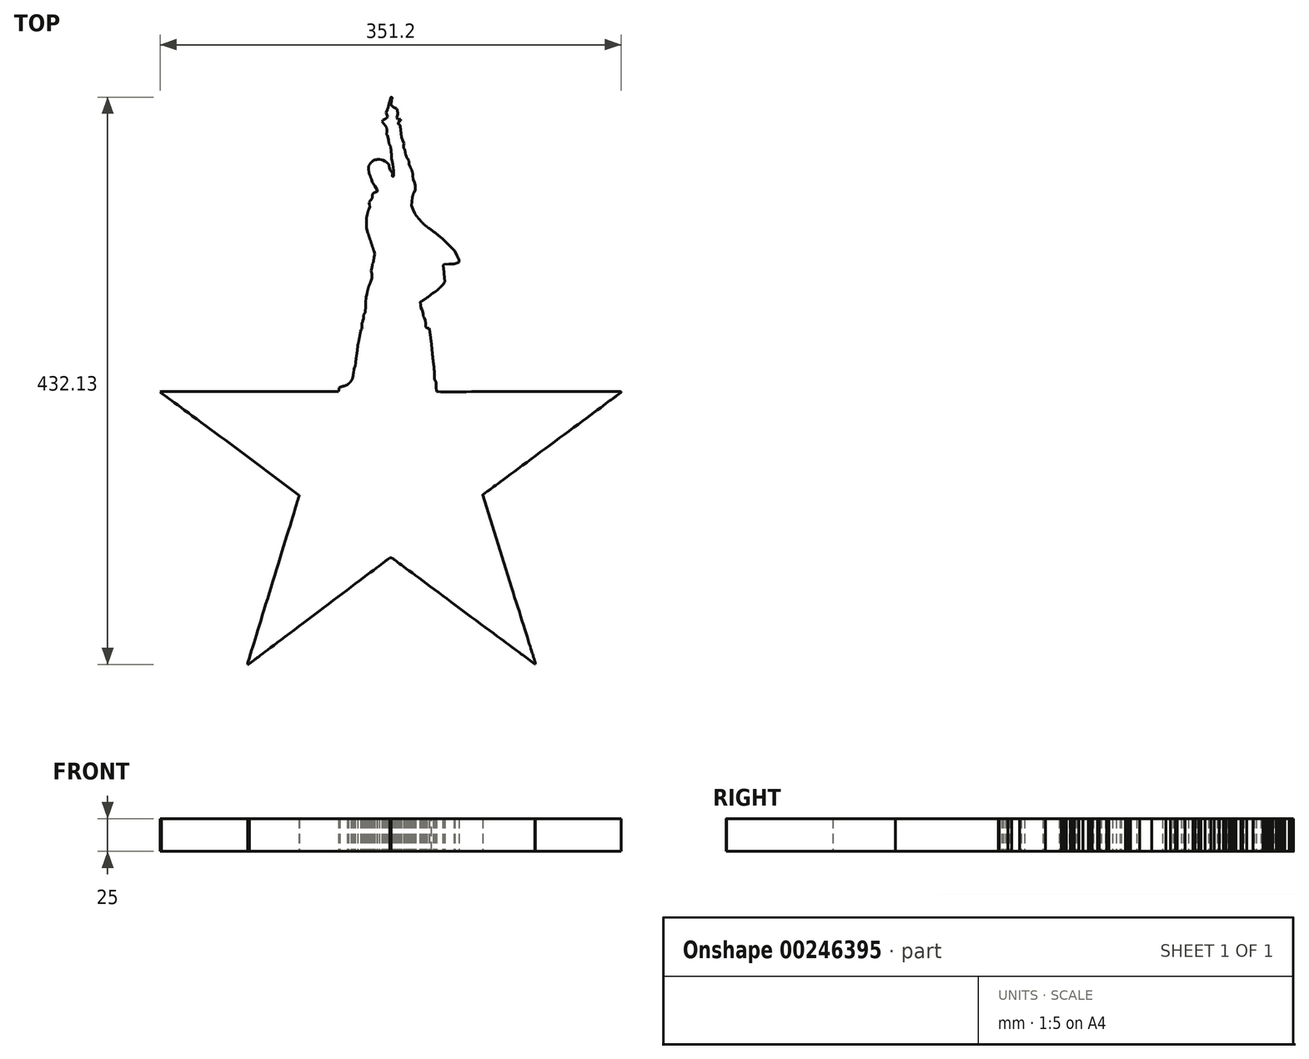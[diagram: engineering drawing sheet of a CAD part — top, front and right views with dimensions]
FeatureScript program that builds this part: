
annotation { "Feature Type Name" : "Feature", "Feature Type Description" : "" }
export const myFeature = defineFeature(function(context is Context, id is Id, definition is map)
    precondition{}
    {
        {
            var Q0;
            Q0=qCreatedBy(makeId("Top.planeOp"),FACE);
            var sketch = newSketch(context, id + "F0", { "sketchPlane" : qUnion([Q0])});
            skFitSpline(sketch, "E0", {"points": [v(0.01, 215.25) * mm, v(-0.13, 214.87) * mm, v(-0.43, 213.8) * mm, v(-0.75, 212.7) * mm]});
            skFitSpline(sketch, "E1", {"points": [v(-0.75, 212.7) * mm, v(-1.07, 211.6) * mm, v(-1.41, 210.33) * mm, v(-1.5, 209.87) * mm]});
            skFitSpline(sketch, "E2", {"points": [v(-1.5, 209.87) * mm, v(-1.6, 209.4) * mm, v(-2.07, 207.96) * mm, v(-2.55, 206.67) * mm]});
            skLineSegment(sketch, "E3", {"start": v(-2.55, 206.67) * mm, "end": v(-3.44, 204.33) * mm});
            skLineSegment(sketch, "E4", {"start": v(-3.44, 204.33) * mm, "end": v(-2.8, 202.77) * mm});
            skLineSegment(sketch, "E5", {"start": v(-2.8, 202.77) * mm, "end": v(-2.15, 201.2) * mm});
            skLineSegment(sketch, "E6", {"start": v(-2.15, 201.2) * mm, "end": v(-2.73, 200.62) * mm});
            skFitSpline(sketch, "E7", {"points": [v(-2.73, 200.62) * mm, v(-3.05, 200.3) * mm, v(-3.9, 199.71) * mm, v(-4.64, 199.3) * mm]});
            skLineSegment(sketch, "E8", {"start": v(-4.64, 199.3) * mm, "end": v(-5.98, 198.58) * mm});
            skLineSegment(sketch, "E9", {"start": v(-5.98, 198.58) * mm, "end": v(-6.28, 198.1) * mm});
            skLineSegment(sketch, "E10", {"start": v(-6.28, 198.1) * mm, "end": v(-6.57, 197.62) * mm});
            skLineSegment(sketch, "E11", {"start": v(-6.57, 197.62) * mm, "end": v(-5.95, 196.95) * mm});
            skFitSpline(sketch, "E12", {"points": [v(-5.95, 196.95) * mm, v(-5.6, 196.58) * mm, v(-5.32, 196.17) * mm, v(-5.32, 196.05) * mm]});
            skFitSpline(sketch, "E13", {"points": [v(-5.32, 196.05) * mm, v(-5.32, 195.92) * mm, v(-4.82, 195.27) * mm, v(-4.21, 194.6) * mm]});
            skLineSegment(sketch, "E14", {"start": v(-4.21, 194.6) * mm, "end": v(-3.1, 193.4) * mm});
            skLineSegment(sketch, "E15", {"start": v(-3.1, 193.4) * mm, "end": v(-2.9, 192.36) * mm});
            skLineSegment(sketch, "E16", {"start": v(-2.9, 192.36) * mm, "end": v(-2.71, 191.32) * mm});
            skLineSegment(sketch, "E17", {"start": v(-2.71, 191.32) * mm, "end": v(-2.86, 189.64) * mm});
            skLineSegment(sketch, "E18", {"start": v(-2.86, 189.64) * mm, "end": v(-3.01, 187.98) * mm});
            skLineSegment(sketch, "E19", {"start": v(-3.01, 187.98) * mm, "end": v(-2.59, 187.11) * mm});
            skLineSegment(sketch, "E20", {"start": v(-2.59, 187.11) * mm, "end": v(-2.16, 186.25) * mm});
            skLineSegment(sketch, "E21", {"start": v(-2.16, 186.25) * mm, "end": v(-1.67, 183.35) * mm});
            skLineSegment(sketch, "E22", {"start": v(-1.67, 183.35) * mm, "end": v(-1.19, 180.45) * mm});
            skLineSegment(sketch, "E23", {"start": v(-1.19, 180.45) * mm, "end": v(-0.6, 179.5) * mm});
            skLineSegment(sketch, "E24", {"start": v(-0.6, 179.5) * mm, "end": v(0, 178.54) * mm});
            skLineSegment(sketch, "E25", {"start": v(0, 178.54) * mm, "end": v(0.32, 175.15) * mm});
            skFitSpline(sketch, "E26", {"points": [v(0.32, 175.15) * mm, v(0.5, 173.3) * mm, v(0.63, 171.21) * mm, v(0.61, 170.54) * mm]});
            skLineSegment(sketch, "E27", {"start": v(0.61, 170.54) * mm, "end": v(0.58, 169.31) * mm});
            skLineSegment(sketch, "E28", {"start": v(0.58, 169.31) * mm, "end": v(1, 167.86) * mm});
            skFitSpline(sketch, "E29", {"points": [v(1, 167.86) * mm, v(1.23, 167.06) * mm, v(1.62, 164.9) * mm, v(1.87, 163.08) * mm]});
            skLineSegment(sketch, "E30", {"start": v(1.87, 163.08) * mm, "end": v(2.33, 159.75) * mm});
            skLineSegment(sketch, "E31", {"start": v(2.33, 159.75) * mm, "end": v(2.2, 157.78) * mm});
            skFitSpline(sketch, "E32", {"points": [v(2.2, 157.78) * mm, v(2.14, 156.69) * mm, v(2.01, 155.72) * mm, v(1.93, 155.64) * mm]});
            skLineSegment(sketch, "E33", {"start": v(1.93, 155.64) * mm, "end": v(1.77, 155.48) * mm});
            skLineSegment(sketch, "E34", {"start": v(1.77, 155.48) * mm, "end": v(1.47, 155.66) * mm});
            skLineSegment(sketch, "E35", {"start": v(1.47, 155.66) * mm, "end": v(1.17, 155.85) * mm});
            skLineSegment(sketch, "E36", {"start": v(1.17, 155.85) * mm, "end": v(1.34, 156.92) * mm});
            skLineSegment(sketch, "E37", {"start": v(1.34, 156.92) * mm, "end": v(1.51, 158) * mm});
            skLineSegment(sketch, "E38", {"start": v(1.51, 158) * mm, "end": v(1.16, 158.67) * mm});
            skFitSpline(sketch, "E39", {"points": [v(1.16, 158.67) * mm, v(0.97, 159.04) * mm, v(0.58, 159.6) * mm, v(0.3, 159.91) * mm]});
            skLineSegment(sketch, "E40", {"start": v(0.3, 159.91) * mm, "end": v(-0.22, 160.49) * mm});
            skLineSegment(sketch, "E41", {"start": v(-0.22, 160.49) * mm, "end": v(-0.79, 162.31) * mm});
            skFitSpline(sketch, "E42", {"points": [v(-0.79, 162.31) * mm, v(-1.1, 163.32) * mm, v(-1.37, 164.34) * mm, v(-1.37, 164.59) * mm]});
            skLineSegment(sketch, "E43", {"start": v(-1.37, 164.59) * mm, "end": v(-1.37, 165.03) * mm});
            skLineSegment(sketch, "E44", {"start": v(-1.37, 165.03) * mm, "end": v(-2.15, 165.72) * mm});
            skFitSpline(sketch, "E45", {"points": [v(-2.15, 165.72) * mm, v(-2.57, 166.1) * mm, v(-3.52, 166.82) * mm, v(-4.24, 167.32) * mm]});
            skLineSegment(sketch, "E46", {"start": v(-4.24, 167.32) * mm, "end": v(-5.55, 168.23) * mm});
            skLineSegment(sketch, "E47", {"start": v(-5.55, 168.23) * mm, "end": v(-7.02, 168.55) * mm});
            skLineSegment(sketch, "E48", {"start": v(-7.02, 168.55) * mm, "end": v(-8.5, 168.86) * mm});
            skLineSegment(sketch, "E49", {"start": v(-8.5, 168.86) * mm, "end": v(-10.2, 168.67) * mm});
            skFitSpline(sketch, "E50", {"points": [v(-10.2, 168.67) * mm, v(-11.11, 168.57) * mm, v(-12.2, 168.36) * mm, v(-12.62, 168.2) * mm]});
            skLineSegment(sketch, "E51", {"start": v(-12.62, 168.2) * mm, "end": v(-13.37, 167.92) * mm});
            skLineSegment(sketch, "E52", {"start": v(-13.37, 167.92) * mm, "end": v(-14.3, 167.02) * mm});
            skFitSpline(sketch, "E53", {"points": [v(-14.3, 167.02) * mm, v(-14.81, 166.53) * mm, v(-15.56, 165.55) * mm, v(-15.98, 164.85) * mm]});
            skLineSegment(sketch, "E54", {"start": v(-15.98, 164.85) * mm, "end": v(-16.73, 163.58) * mm});
            skLineSegment(sketch, "E55", {"start": v(-16.73, 163.58) * mm, "end": v(-16.66, 161.07) * mm});
            skLineSegment(sketch, "E56", {"start": v(-16.66, 161.07) * mm, "end": v(-16.6, 158.55) * mm});
            skLineSegment(sketch, "E57", {"start": v(-16.6, 158.55) * mm, "end": v(-16.06, 157.26) * mm});
            skFitSpline(sketch, "E58", {"points": [v(-16.06, 157.26) * mm, v(-15.76, 156.54) * mm, v(-15.12, 154.95) * mm, v(-14.65, 153.7) * mm]});
            skLineSegment(sketch, "E59", {"start": v(-14.65, 153.7) * mm, "end": v(-13.8, 151.45) * mm});
            skLineSegment(sketch, "E60", {"start": v(-13.8, 151.45) * mm, "end": v(-12.09, 148.62) * mm});
            skLineSegment(sketch, "E61", {"start": v(-12.09, 148.62) * mm, "end": v(-10.36, 145.8) * mm});
            skLineSegment(sketch, "E62", {"start": v(-10.36, 145.8) * mm, "end": v(-10.2, 145.03) * mm});
            skLineSegment(sketch, "E63", {"start": v(-10.2, 145.03) * mm, "end": v(-10.05, 144.26) * mm});
            skLineSegment(sketch, "E64", {"start": v(-10.05, 144.26) * mm, "end": v(-10.44, 144.13) * mm});
            skFitSpline(sketch, "E65", {"points": [v(-10.44, 144.13) * mm, v(-10.65, 144.07) * mm, v(-11.14, 143.94) * mm, v(-11.53, 143.85) * mm]});
            skLineSegment(sketch, "E66", {"start": v(-11.53, 143.85) * mm, "end": v(-12.24, 143.7) * mm});
            skLineSegment(sketch, "E67", {"start": v(-12.24, 143.7) * mm, "end": v(-13.01, 142.97) * mm});
            skLineSegment(sketch, "E68", {"start": v(-13.01, 142.97) * mm, "end": v(-13.79, 142.25) * mm});
            skLineSegment(sketch, "E69", {"start": v(-13.79, 142.25) * mm, "end": v(-13.79, 140.73) * mm});
            skLineSegment(sketch, "E70", {"start": v(-13.79, 140.73) * mm, "end": v(-13.79, 139.21) * mm});
            skLineSegment(sketch, "E71", {"start": v(-13.79, 139.21) * mm, "end": v(-15.08, 137.7) * mm});
            skLineSegment(sketch, "E72", {"start": v(-15.08, 137.7) * mm, "end": v(-16.36, 136.2) * mm});
            skLineSegment(sketch, "E73", {"start": v(-16.36, 136.2) * mm, "end": v(-16.19, 134.36) * mm});
            skLineSegment(sketch, "E74", {"start": v(-16.19, 134.36) * mm, "end": v(-16, 132.53) * mm});
            skLineSegment(sketch, "E75", {"start": v(-16, 132.53) * mm, "end": v(-16.58, 130.98) * mm});
            skFitSpline(sketch, "E76", {"points": [v(-16.58, 130.98) * mm, v(-16.9, 130.12) * mm, v(-17.44, 128.29) * mm, v(-17.78, 126.9) * mm]});
            skLineSegment(sketch, "E77", {"start": v(-17.78, 126.9) * mm, "end": v(-18.4, 124.35) * mm});
            skLineSegment(sketch, "E78", {"start": v(-18.4, 124.35) * mm, "end": v(-18.42, 120.4) * mm});
            skLineSegment(sketch, "E79", {"start": v(-18.42, 120.4) * mm, "end": v(-18.45, 116.45) * mm});
            skLineSegment(sketch, "E80", {"start": v(-18.45, 116.45) * mm, "end": v(-17.35, 112.92) * mm});
            skFitSpline(sketch, "E81", {"points": [v(-17.35, 112.92) * mm, v(-16.75, 110.98) * mm, v(-15.63, 107.55) * mm, v(-14.87, 105.3) * mm]});
            skFitSpline(sketch, "E82", {"points": [v(-14.87, 105.3) * mm, v(-14.12, 103.05) * mm, v(-13.18, 100.2) * mm, v(-12.8, 98.99) * mm]});
            skLineSegment(sketch, "E83", {"start": v(-12.8, 98.99) * mm, "end": v(-12.1, 96.77) * mm});
            skLineSegment(sketch, "E84", {"start": v(-12.1, 96.77) * mm, "end": v(-12.54, 94.05) * mm});
            skLineSegment(sketch, "E85", {"start": v(-12.54, 94.05) * mm, "end": v(-12.96, 91.33) * mm});
            skLineSegment(sketch, "E86", {"start": v(-12.96, 91.33) * mm, "end": v(-13.43, 90.2) * mm});
            skLineSegment(sketch, "E87", {"start": v(-13.43, 90.2) * mm, "end": v(-13.89, 89.08) * mm});
            skLineSegment(sketch, "E88", {"start": v(-13.89, 89.08) * mm, "end": v(-14.08, 87.52) * mm});
            skFitSpline(sketch, "E89", {"points": [v(-14.08, 87.52) * mm, v(-14.19, 86.67) * mm, v(-14.45, 85.56) * mm, v(-14.66, 85.05) * mm]});
            skLineSegment(sketch, "E90", {"start": v(-14.66, 85.05) * mm, "end": v(-15.04, 84.15) * mm});
            skLineSegment(sketch, "E91", {"start": v(-15.04, 84.15) * mm, "end": v(-14.64, 82.8) * mm});
            skLineSegment(sketch, "E92", {"start": v(-14.64, 82.8) * mm, "end": v(-14.22, 81.46) * mm});
            skLineSegment(sketch, "E93", {"start": v(-14.22, 81.46) * mm, "end": v(-14.27, 79.87) * mm});
            skLineSegment(sketch, "E94", {"start": v(-14.27, 79.87) * mm, "end": v(-14.33, 78.29) * mm});
            skLineSegment(sketch, "E95", {"start": v(-14.33, 78.29) * mm, "end": v(-15.03, 76.25) * mm});
            skFitSpline(sketch, "E96", {"points": [v(-15.03, 76.25) * mm, v(-15.42, 75.13) * mm, v(-15.99, 73.7) * mm, v(-16.29, 73.04) * mm]});
            skFitSpline(sketch, "E97", {"points": [v(-16.29, 73.04) * mm, v(-16.58, 72.4) * mm, v(-17.06, 70.9) * mm, v(-17.33, 69.74) * mm]});
            skFitSpline(sketch, "E98", {"points": [v(-17.33, 69.74) * mm, v(-17.6, 68.58) * mm, v(-17.99, 66.8) * mm, v(-18.2, 65.8) * mm]});
            skLineSegment(sketch, "E99", {"start": v(-18.2, 65.8) * mm, "end": v(-18.6, 63.96) * mm});
            skLineSegment(sketch, "E100", {"start": v(-18.6, 63.96) * mm, "end": v(-18.89, 59.44) * mm});
            skFitSpline(sketch, "E101", {"points": [v(-18.89, 59.44) * mm, v(-19.04, 56.96) * mm, v(-19.2, 54.28) * mm, v(-19.25, 53.49) * mm]});
            skLineSegment(sketch, "E102", {"start": v(-19.25, 53.49) * mm, "end": v(-19.32, 52.05) * mm});
            skLineSegment(sketch, "E103", {"start": v(-19.32, 52.05) * mm, "end": v(-19.95, 51.27) * mm});
            skLineSegment(sketch, "E104", {"start": v(-19.95, 51.27) * mm, "end": v(-20.56, 50.47) * mm});
            skLineSegment(sketch, "E105", {"start": v(-20.56, 50.47) * mm, "end": v(-20.56, 49) * mm});
            skLineSegment(sketch, "E106", {"start": v(-20.56, 49) * mm, "end": v(-20.56, 47.5) * mm});
            skLineSegment(sketch, "E107", {"start": v(-20.56, 47.5) * mm, "end": v(-20.99, 46.7) * mm});
            skFitSpline(sketch, "E108", {"points": [v(-20.99, 46.7) * mm, v(-21.22, 46.25) * mm, v(-21.4, 45.66) * mm, v(-21.4, 45.38) * mm]});
            skFitSpline(sketch, "E109", {"points": [v(-21.4, 45.38) * mm, v(-21.41, 45.1) * mm, v(-21.53, 44.63) * mm, v(-21.68, 44.35) * mm]});
            skFitSpline(sketch, "E110", {"points": [v(-21.68, 44.35) * mm, v(-21.83, 44.07) * mm, v(-21.98, 43.47) * mm, v(-22, 43.03) * mm]});
            skFitSpline(sketch, "E111", {"points": [v(-22, 43.03) * mm, v(-22.02, 42.58) * mm, v(-21.95, 41.62) * mm, v(-21.85, 40.9) * mm]});
            skLineSegment(sketch, "E112", {"start": v(-21.85, 40.9) * mm, "end": v(-21.66, 39.57) * mm});
            skLineSegment(sketch, "E113", {"start": v(-21.66, 39.57) * mm, "end": v(-22.21, 39.28) * mm});
            skLineSegment(sketch, "E114", {"start": v(-22.21, 39.28) * mm, "end": v(-22.76, 38.99) * mm});
            skLineSegment(sketch, "E115", {"start": v(-22.76, 38.99) * mm, "end": v(-22.95, 37.65) * mm});
            skFitSpline(sketch, "E116", {"points": [v(-22.95, 37.65) * mm, v(-23.06, 36.9) * mm, v(-23.51, 34.41) * mm, v(-23.97, 32.11) * mm]});
            skFitSpline(sketch, "E117", {"points": [v(-23.97, 32.11) * mm, v(-24.42, 29.8) * mm, v(-24.85, 27.83) * mm, v(-24.91, 27.73) * mm]});
            skFitSpline(sketch, "E118", {"points": [v(-24.91, 27.73) * mm, v(-24.97, 27.62) * mm, v(-25.1, 26.59) * mm, v(-25.21, 25.43) * mm]});
            skFitSpline(sketch, "E119", {"points": [v(-25.21, 25.43) * mm, v(-25.31, 24.26) * mm, v(-25.63, 21.72) * mm, v(-25.92, 19.77) * mm]});
            skFitSpline(sketch, "E120", {"points": [v(-25.92, 19.77) * mm, v(-26.22, 17.82) * mm, v(-26.6, 15.13) * mm, v(-26.76, 13.8) * mm]});
            skLineSegment(sketch, "E121", {"start": v(-26.76, 13.8) * mm, "end": v(-27.06, 11.36) * mm});
            skLineSegment(sketch, "E122", {"start": v(-27.06, 11.36) * mm, "end": v(-27.49, 10.16) * mm});
            skLineSegment(sketch, "E123", {"start": v(-27.49, 10.16) * mm, "end": v(-27.9, 8.96) * mm});
            skLineSegment(sketch, "E124", {"start": v(-27.9, 8.96) * mm, "end": v(-28.34, 5.98) * mm});
            skFitSpline(sketch, "E125", {"points": [v(-28.34, 5.98) * mm, v(-28.58, 4.34) * mm, v(-28.9, 2.57) * mm, v(-29.07, 2.04) * mm]});
            skFitSpline(sketch, "E126", {"points": [v(-29.07, 2.04) * mm, v(-29.24, 1.52) * mm, v(-29.68, 0.64) * mm, v(-30.06, 0.07) * mm]});
            skFitSpline(sketch, "E127", {"points": [v(-30.06, 0.07) * mm, v(-30.44, -0.5) * mm, v(-31.29, -1.43) * mm, v(-31.94, -2.01) * mm]});
            skLineSegment(sketch, "E128", {"start": v(-31.94, -2.01) * mm, "end": v(-33.12, -3.07) * mm});
            skLineSegment(sketch, "E129", {"start": v(-33.12, -3.07) * mm, "end": v(-35.52, -3.78) * mm});
            skFitSpline(sketch, "E130", {"points": [v(-35.52, -3.78) * mm, v(-36.84, -4.18) * mm, v(-38.24, -4.68) * mm, v(-38.62, -4.9) * mm]});
            skLineSegment(sketch, "E131", {"start": v(-38.62, -4.9) * mm, "end": v(-39.33, -5.3) * mm});
            skLineSegment(sketch, "E132", {"start": v(-39.33, -5.3) * mm, "end": v(-39.4, -6.09) * mm});
            skFitSpline(sketch, "E133", {"points": [v(-39.4, -6.09) * mm, v(-39.45, -6.53) * mm, v(-39.55, -7.16) * mm, v(-39.62, -7.5) * mm]});
            skLineSegment(sketch, "E134", {"start": v(-39.62, -7.5) * mm, "end": v(-39.75, -8.1) * mm});
            skLineSegment(sketch, "E135", {"start": v(-39.75, -8.1) * mm, "end": v(-106.98, -8.02) * mm});
            skLineSegment(sketch, "E136", {"start": v(-106.98, -8.02) * mm, "end": v(-174.19, -7.92) * mm});
            skLineSegment(sketch, "E137", {"start": v(-174.19, -7.92) * mm, "end": v(-174.9, -8.2) * mm});
            skLineSegment(sketch, "E138", {"start": v(-174.9, -8.2) * mm, "end": v(-175.6, -8.46) * mm});
            skLineSegment(sketch, "E139", {"start": v(-175.6, -8.46) * mm, "end": v(-174.57, -9.31) * mm});
            skFitSpline(sketch, "E140", {"points": [v(-174.57, -9.31) * mm, v(-174, -9.78) * mm, v(-172.48, -10.87) * mm, v(-122.38, -47.81) * mm]});
            skLineSegment(sketch, "E141", {"start": v(-69.67, -86.7) * mm, "end": v(-69.67, -87.08) * mm});
            skFitSpline(sketch, "E142", {"points": [v(-69.67, -87.08) * mm, v(-69.67, -87.3) * mm, v(-69.91, -88.2) * mm, v(-70.2, -89.1) * mm]});
            skFitSpline(sketch, "E143", {"points": [v(-70.2, -89.1) * mm, v(-70.5, -89.98) * mm, v(-71.01, -91.73) * mm, v(-89.77, -152.77) * mm]});
            skFitSpline(sketch, "E144", {"points": [v(-89.77, -152.77) * mm, v(-108.53, -213.82) * mm, v(-108.9, -215.18) * mm, v(-108.9, -215.43) * mm]});
            skLineSegment(sketch, "E145", {"start": v(-108.9, -215.43) * mm, "end": v(-108.9, -215.87) * mm});
            skLineSegment(sketch, "E146", {"start": v(-108.9, -215.87) * mm, "end": v(-108.69, -215.87) * mm});
            skFitSpline(sketch, "E147", {"points": [v(-108.69, -215.87) * mm, v(-108.57, -215.86) * mm, v(-108.14, -215.64) * mm, v(-107.72, -215.37) * mm]});
            skFitSpline(sketch, "E148", {"points": [v(-107.72, -215.37) * mm, v(-107.3, -215.1) * mm, v(-105.26, -213.6) * mm, v(-103.2, -212.04) * mm]});
            skFitSpline(sketch, "E149", {"points": [v(-103.2, -212.04) * mm, v(-101.14, -210.48) * mm, v(-97.94, -208.06) * mm, v(-50.88, -172.6) * mm]});
            skFitSpline(sketch, "E150", {"points": [v(-50.88, -172.6) * mm, v(-3.81, -137.14) * mm, v(-2.53, -136.15) * mm, v(-1.88, -135.6) * mm]});
            skLineSegment(sketch, "E151", {"start": v(-1.88, -135.6) * mm, "end": v(-0.7, -134.59) * mm});
            skLineSegment(sketch, "E152", {"start": v(-0.7, -134.59) * mm, "end": v(-0.12, -134.59) * mm});
            skLineSegment(sketch, "E153", {"start": v(-0.12, -134.59) * mm, "end": v(0.47, -134.59) * mm});
            skLineSegment(sketch, "E154", {"start": v(0.47, -134.59) * mm, "end": v(1.78, -135.5) * mm});
            skFitSpline(sketch, "E155", {"points": [v(1.78, -135.5) * mm, v(2.5, -136) * mm, v(3.86, -137) * mm, v(46.01, -168.3) * mm]});
            skFitSpline(sketch, "E156", {"points": [v(46.01, -168.3) * mm, v(88.17, -199.6) * mm, v(95.45, -205.03) * mm, v(100.6, -208.86) * mm]});
            skLineSegment(sketch, "E157", {"start": v(100.6, -208.86) * mm, "end": v(109.94, -215.83) * mm});
            skLineSegment(sketch, "E158", {"start": v(109.94, -215.83) * mm, "end": v(110.14, -215.7) * mm});
            skLineSegment(sketch, "E159", {"start": v(110.14, -215.7) * mm, "end": v(110.34, -215.58) * mm});
            skLineSegment(sketch, "E160", {"start": v(110.34, -215.58) * mm, "end": v(110.12, -214.8) * mm});
            skFitSpline(sketch, "E161", {"points": [v(110.12, -214.8) * mm, v(109.99, -214.38) * mm, v(109.56, -212.95) * mm, v(109.17, -211.63) * mm]});
            skFitSpline(sketch, "E162", {"points": [v(109.17, -211.63) * mm, v(108.78, -210.31) * mm, v(106.85, -204.09) * mm, v(92.08, -157.19) * mm]});
            skLineSegment(sketch, "E163", {"start": v(70.05, -87.16) * mm, "end": v(70.2, -86.82) * mm});
            skFitSpline(sketch, "E164", {"points": [v(70.2, -86.82) * mm, v(70.28, -86.63) * mm, v(71.68, -85.51) * mm, v(73.32, -84.35) * mm]});
            skFitSpline(sketch, "E165", {"points": [v(73.32, -84.35) * mm, v(74.96, -83.19) * mm, v(77.04, -81.66) * mm, v(121.31, -48.87) * mm]});
            skFitSpline(sketch, "E166", {"points": [v(121.31, -48.87) * mm, v(165.59, -16.07) * mm, v(170.07, -12.76) * mm, v(172.04, -11.32) * mm]});
            skLineSegment(sketch, "E167", {"start": v(172.04, -11.32) * mm, "end": v(175.6, -8.7) * mm});
            skLineSegment(sketch, "E168", {"start": v(175.6, -8.7) * mm, "end": v(175.44, -8.43) * mm});
            skLineSegment(sketch, "E169", {"start": v(175.44, -8.43) * mm, "end": v(175.27, -8.17) * mm});
            skLineSegment(sketch, "E170", {"start": v(175.27, -8.17) * mm, "end": v(105.26, -8.16) * mm});
            skFitSpline(sketch, "E171", {"points": [v(105.26, -8.16) * mm, v(66.76, -8.15) * mm, v(35.17, -8.09) * mm, v(35.05, -8.02) * mm]});
            skLineSegment(sketch, "E172", {"start": v(35.05, -8.02) * mm, "end": v(34.84, -7.9) * mm});
            skLineSegment(sketch, "E173", {"start": v(34.84, -7.9) * mm, "end": v(34.67, -4.55) * mm});
            skLineSegment(sketch, "E174", {"start": v(34.67, -4.55) * mm, "end": v(34.5, -1.22) * mm});
            skLineSegment(sketch, "E175", {"start": v(34.5, -1.22) * mm, "end": v(34.01, 0.18) * mm});
            skLineSegment(sketch, "E176", {"start": v(34.01, 0.18) * mm, "end": v(33.52, 1.59) * mm});
            skLineSegment(sketch, "E177", {"start": v(33.52, 1.59) * mm, "end": v(33.47, 3.28) * mm});
            skFitSpline(sketch, "E178", {"points": [v(33.47, 3.28) * mm, v(33.45, 4.21) * mm, v(33.34, 6.18) * mm, v(33.24, 7.65) * mm]});
            skFitSpline(sketch, "E179", {"points": [v(33.24, 7.65) * mm, v(33.13, 9.13) * mm, v(32.92, 11.16) * mm, v(32.78, 12.17) * mm]});
            skFitSpline(sketch, "E180", {"points": [v(32.78, 12.17) * mm, v(32.63, 13.18) * mm, v(32.39, 15.15) * mm, v(32.23, 16.54) * mm]});
            skFitSpline(sketch, "E181", {"points": [v(32.23, 16.54) * mm, v(32.07, 17.94) * mm, v(31.8, 20.55) * mm, v(31.63, 22.33) * mm]});
            skFitSpline(sketch, "E182", {"points": [v(31.63, 22.33) * mm, v(31.46, 24.11) * mm, v(31.27, 26.34) * mm, v(31.19, 27.27) * mm]});
            skFitSpline(sketch, "E183", {"points": [v(31.19, 27.27) * mm, v(31.11, 28.2) * mm, v(30.74, 31.18) * mm, v(30.35, 33.9) * mm]});
            skFitSpline(sketch, "E184", {"points": [v(30.35, 33.9) * mm, v(29.97, 36.62) * mm, v(29.58, 39.13) * mm, v(29.49, 39.47) * mm]});
            skLineSegment(sketch, "E185", {"start": v(29.49, 39.47) * mm, "end": v(29.33, 40.1) * mm});
            skLineSegment(sketch, "E186", {"start": v(29.33, 40.1) * mm, "end": v(28.54, 40.1) * mm});
            skLineSegment(sketch, "E187", {"start": v(28.54, 40.1) * mm, "end": v(27.73, 40.1) * mm});
            skLineSegment(sketch, "E188", {"start": v(27.73, 40.1) * mm, "end": v(27.3, 40.55) * mm});
            skFitSpline(sketch, "E189", {"points": [v(27.3, 40.55) * mm, v(27.05, 40.8) * mm, v(26.84, 41.2) * mm, v(26.82, 41.47) * mm]});
            skFitSpline(sketch, "E190", {"points": [v(26.82, 41.47) * mm, v(26.8, 41.73) * mm, v(26.75, 42.58) * mm, v(26.7, 43.36) * mm]});
            skFitSpline(sketch, "E191", {"points": [v(26.7, 43.36) * mm, v(26.67, 44.13) * mm, v(26.47, 45.47) * mm, v(26.25, 46.32) * mm]});
            skLineSegment(sketch, "E192", {"start": v(26.25, 46.32) * mm, "end": v(25.86, 47.87) * mm});
            skLineSegment(sketch, "E193", {"start": v(25.86, 47.87) * mm, "end": v(25.35, 48.62) * mm});
            skLineSegment(sketch, "E194", {"start": v(25.35, 48.62) * mm, "end": v(24.84, 49.38) * mm});
            skLineSegment(sketch, "E195", {"start": v(24.84, 49.38) * mm, "end": v(24.68, 51.02) * mm});
            skLineSegment(sketch, "E196", {"start": v(24.68, 51.02) * mm, "end": v(24.52, 52.67) * mm});
            skLineSegment(sketch, "E197", {"start": v(24.52, 52.67) * mm, "end": v(23.75, 54.36) * mm});
            skLineSegment(sketch, "E198", {"start": v(23.75, 54.36) * mm, "end": v(22.96, 56.06) * mm});
            skLineSegment(sketch, "E199", {"start": v(22.96, 56.06) * mm, "end": v(22.78, 58.1) * mm});
            skLineSegment(sketch, "E200", {"start": v(22.78, 58.1) * mm, "end": v(22.58, 60.15) * mm});
            skLineSegment(sketch, "E201", {"start": v(22.58, 60.15) * mm, "end": v(23.66, 60.77) * mm});
            skFitSpline(sketch, "E202", {"points": [v(23.66, 60.77) * mm, v(24.25, 61.12) * mm, v(25.75, 62.1) * mm, v(27, 62.93) * mm]});
            skFitSpline(sketch, "E203", {"points": [v(27, 62.93) * mm, v(28.23, 63.78) * mm, v(29.77, 64.94) * mm, v(30.41, 65.53) * mm]});
            skFitSpline(sketch, "E204", {"points": [v(30.41, 65.53) * mm, v(31.06, 66.11) * mm, v(31.97, 66.79) * mm, v(32.45, 67.04) * mm]});
            skFitSpline(sketch, "E205", {"points": [v(32.45, 67.04) * mm, v(32.93, 67.28) * mm, v(33.74, 67.78) * mm, v(34.25, 68.13) * mm]});
            skFitSpline(sketch, "E206", {"points": [v(34.25, 68.13) * mm, v(34.76, 68.48) * mm, v(36.34, 69.93) * mm, v(37.77, 71.35) * mm]});
            skLineSegment(sketch, "E207", {"start": v(37.77, 71.35) * mm, "end": v(40.35, 73.92) * mm});
            skLineSegment(sketch, "E208", {"start": v(40.35, 73.92) * mm, "end": v(40.79, 74.76) * mm});
            skLineSegment(sketch, "E209", {"start": v(40.79, 74.76) * mm, "end": v(41.22, 75.6) * mm});
            skLineSegment(sketch, "E210", {"start": v(41.22, 75.6) * mm, "end": v(40.94, 78.94) * mm});
            skFitSpline(sketch, "E211", {"points": [v(40.94, 78.94) * mm, v(40.78, 80.79) * mm, v(40.54, 83.64) * mm, v(40.4, 85.27) * mm]});
            skLineSegment(sketch, "E212", {"start": v(40.4, 85.27) * mm, "end": v(40.16, 88.22) * mm});
            skLineSegment(sketch, "E213", {"start": v(40.16, 88.22) * mm, "end": v(40.42, 88.54) * mm});
            skLineSegment(sketch, "E214", {"start": v(40.42, 88.54) * mm, "end": v(40.67, 88.85) * mm});
            skLineSegment(sketch, "E215", {"start": v(40.67, 88.85) * mm, "end": v(44.45, 89.01) * mm});
            skLineSegment(sketch, "E216", {"start": v(44.45, 89.01) * mm, "end": v(48.22, 89.18) * mm});
            skLineSegment(sketch, "E217", {"start": v(48.22, 89.18) * mm, "end": v(50.16, 89.83) * mm});
            skLineSegment(sketch, "E218", {"start": v(50.16, 89.83) * mm, "end": v(52.1, 90.49) * mm});
            skLineSegment(sketch, "E219", {"start": v(52.1, 90.49) * mm, "end": v(52.07, 91.36) * mm});
            skLineSegment(sketch, "E220", {"start": v(52.07, 91.36) * mm, "end": v(52.03, 92.23) * mm});
            skLineSegment(sketch, "E221", {"start": v(52.03, 92.23) * mm, "end": v(50.4, 95.6) * mm});
            skLineSegment(sketch, "E222", {"start": v(50.4, 95.6) * mm, "end": v(48.76, 98.95) * mm});
            skLineSegment(sketch, "E223", {"start": v(48.76, 98.95) * mm, "end": v(44.23, 103.57) * mm});
            skLineSegment(sketch, "E224", {"start": v(44.23, 103.57) * mm, "end": v(39.7, 108.18) * mm});
            skLineSegment(sketch, "E225", {"start": v(39.7, 108.18) * mm, "end": v(36.3, 110.93) * mm});
            skFitSpline(sketch, "E226", {"points": [v(36.3, 110.93) * mm, v(34.44, 112.44) * mm, v(31.46, 114.73) * mm, v(29.67, 116) * mm]});
            skFitSpline(sketch, "E227", {"points": [v(29.67, 116) * mm, v(27.89, 117.3) * mm, v(26.05, 118.68) * mm, v(25.58, 119.09) * mm]});
            skFitSpline(sketch, "E228", {"points": [v(25.58, 119.09) * mm, v(25.11, 119.5) * mm, v(23.62, 121.1) * mm, v(22.26, 122.65) * mm]});
            skFitSpline(sketch, "E229", {"points": [v(22.26, 122.65) * mm, v(20.9, 124.2) * mm, v(19.46, 125.93) * mm, v(19.07, 126.5) * mm]});
            skLineSegment(sketch, "E230", {"start": v(19.07, 126.5) * mm, "end": v(18.36, 127.52) * mm});
            skLineSegment(sketch, "E231", {"start": v(18.36, 127.52) * mm, "end": v(17.12, 130.54) * mm});
            skLineSegment(sketch, "E232", {"start": v(17.12, 130.54) * mm, "end": v(15.9, 133.55) * mm});
            skLineSegment(sketch, "E233", {"start": v(15.9, 133.55) * mm, "end": v(16.15, 136.72) * mm});
            skLineSegment(sketch, "E234", {"start": v(16.15, 136.72) * mm, "end": v(16.42, 139.88) * mm});
            skLineSegment(sketch, "E235", {"start": v(16.42, 139.88) * mm, "end": v(16.84, 141.22) * mm});
            skFitSpline(sketch, "E236", {"points": [v(16.84, 141.22) * mm, v(17.08, 141.97) * mm, v(17.59, 143.26) * mm, v(17.97, 144.1) * mm]});
            skLineSegment(sketch, "E237", {"start": v(17.97, 144.1) * mm, "end": v(18.67, 145.63) * mm});
            skLineSegment(sketch, "E238", {"start": v(18.67, 145.63) * mm, "end": v(18.67, 147.32) * mm});
            skLineSegment(sketch, "E239", {"start": v(18.67, 147.32) * mm, "end": v(18.67, 149.01) * mm});
            skLineSegment(sketch, "E240", {"start": v(18.67, 149.01) * mm, "end": v(17.97, 151.22) * mm});
            skLineSegment(sketch, "E241", {"start": v(17.97, 151.22) * mm, "end": v(17.27, 153.42) * mm});
            skLineSegment(sketch, "E242", {"start": v(17.27, 153.42) * mm, "end": v(16.98, 155.97) * mm});
            skFitSpline(sketch, "E243", {"points": [v(16.98, 155.97) * mm, v(16.82, 157.37) * mm, v(16.53, 159.09) * mm, v(16.32, 159.78) * mm]});
            skFitSpline(sketch, "E244", {"points": [v(16.32, 159.78) * mm, v(16.11, 160.47) * mm, v(15.47, 161.91) * mm, v(14.9, 162.98) * mm]});
            skLineSegment(sketch, "E245", {"start": v(14.9, 162.98) * mm, "end": v(13.87, 164.93) * mm});
            skLineSegment(sketch, "E246", {"start": v(13.87, 164.93) * mm, "end": v(13.87, 166.17) * mm});
            skLineSegment(sketch, "E247", {"start": v(13.87, 166.17) * mm, "end": v(13.87, 167.4) * mm});
            skLineSegment(sketch, "E248", {"start": v(13.87, 167.4) * mm, "end": v(13.49, 168.32) * mm});
            skFitSpline(sketch, "E249", {"points": [v(13.49, 168.32) * mm, v(13.28, 168.82) * mm, v(12.9, 169.4) * mm, v(12.66, 169.6) * mm]});
            skLineSegment(sketch, "E250", {"start": v(12.66, 169.6) * mm, "end": v(12.21, 169.97) * mm});
            skLineSegment(sketch, "E251", {"start": v(12.21, 169.97) * mm, "end": v(12.02, 170.87) * mm});
            skFitSpline(sketch, "E252", {"points": [v(12.02, 170.87) * mm, v(11.91, 171.36) * mm, v(11.7, 171.9) * mm, v(11.56, 172.1) * mm]});
            skLineSegment(sketch, "E253", {"start": v(11.56, 172.1) * mm, "end": v(11.3, 172.43) * mm});
            skLineSegment(sketch, "E254", {"start": v(11.3, 172.43) * mm, "end": v(11.02, 174.34) * mm});
            skLineSegment(sketch, "E255", {"start": v(11.02, 174.34) * mm, "end": v(10.75, 176.26) * mm});
            skLineSegment(sketch, "E256", {"start": v(10.75, 176.26) * mm, "end": v(10.36, 176.85) * mm});
            skLineSegment(sketch, "E257", {"start": v(10.36, 176.85) * mm, "end": v(9.97, 177.45) * mm});
            skLineSegment(sketch, "E258", {"start": v(9.97, 177.45) * mm, "end": v(10, 179.12) * mm});
            skLineSegment(sketch, "E259", {"start": v(10, 179.12) * mm, "end": v(10.03, 180.8) * mm});
            skLineSegment(sketch, "E260", {"start": v(10.03, 180.8) * mm, "end": v(9.07, 183.2) * mm});
            skLineSegment(sketch, "E261", {"start": v(9.07, 183.2) * mm, "end": v(8.1, 185.6) * mm});
            skLineSegment(sketch, "E262", {"start": v(8.1, 185.6) * mm, "end": v(7.9, 188.42) * mm});
            skFitSpline(sketch, "E263", {"points": [v(7.9, 188.42) * mm, v(7.78, 189.97) * mm, v(7.57, 192.01) * mm, v(7.42, 192.97) * mm]});
            skFitSpline(sketch, "E264", {"points": [v(7.42, 192.97) * mm, v(7.28, 193.92) * mm, v(7.08, 194.84) * mm, v(6.97, 195.01) * mm]});
            skFitSpline(sketch, "E265", {"points": [v(6.97, 195.01) * mm, v(6.87, 195.19) * mm, v(6.6, 195.33) * mm, v(6.4, 195.33) * mm]});
            skLineSegment(sketch, "E266", {"start": v(6.4, 195.33) * mm, "end": v(6.03, 195.33) * mm});
            skLineSegment(sketch, "E267", {"start": v(6.03, 195.33) * mm, "end": v(5.86, 195.76) * mm});
            skLineSegment(sketch, "E268", {"start": v(5.86, 195.76) * mm, "end": v(5.7, 196.18) * mm});
            skLineSegment(sketch, "E269", {"start": v(5.7, 196.18) * mm, "end": v(5.95, 196.83) * mm});
            skLineSegment(sketch, "E270", {"start": v(5.95, 196.83) * mm, "end": v(6.2, 197.48) * mm});
            skLineSegment(sketch, "E271", {"start": v(6.2, 197.48) * mm, "end": v(6.93, 197.97) * mm});
            skLineSegment(sketch, "E272", {"start": v(6.93, 197.97) * mm, "end": v(7.66, 198.44) * mm});
            skLineSegment(sketch, "E273", {"start": v(7.66, 198.44) * mm, "end": v(7.66, 198.86) * mm});
            skLineSegment(sketch, "E274", {"start": v(7.66, 198.86) * mm, "end": v(7.66, 199.28) * mm});
            skLineSegment(sketch, "E275", {"start": v(7.66, 199.28) * mm, "end": v(7.17, 199.33) * mm});
            skFitSpline(sketch, "E276", {"points": [v(7.17, 199.33) * mm, v(6.9, 199.35) * mm, v(6.4, 199.34) * mm, v(6.08, 199.32) * mm]});
            skLineSegment(sketch, "E277", {"start": v(6.08, 199.32) * mm, "end": v(5.5, 199.27) * mm});
            skLineSegment(sketch, "E278", {"start": v(5.5, 199.27) * mm, "end": v(4.97, 199.85) * mm});
            skLineSegment(sketch, "E279", {"start": v(4.97, 199.85) * mm, "end": v(4.45, 200.43) * mm});
            skLineSegment(sketch, "E280", {"start": v(4.45, 200.43) * mm, "end": v(4.95, 201.84) * mm});
            skLineSegment(sketch, "E281", {"start": v(4.95, 201.84) * mm, "end": v(5.46, 203.25) * mm});
            skLineSegment(sketch, "E282", {"start": v(5.46, 203.25) * mm, "end": v(5.26, 204.87) * mm});
            skFitSpline(sketch, "E283", {"points": [v(5.26, 204.87) * mm, v(5.15, 205.75) * mm, v(4.95, 206.68) * mm, v(4.81, 206.94) * mm]});
            skLineSegment(sketch, "E284", {"start": v(4.81, 206.94) * mm, "end": v(4.56, 207.4) * mm});
            skLineSegment(sketch, "E285", {"start": v(4.56, 207.4) * mm, "end": v(3.78, 207.72) * mm});
            skFitSpline(sketch, "E286", {"points": [v(3.78, 207.72) * mm, v(3.35, 207.9) * mm, v(2.73, 208.2) * mm, v(2.41, 208.4) * mm]});
            skFitSpline(sketch, "E287", {"points": [v(2.41, 208.4) * mm, v(2.09, 208.58) * mm, v(1.6, 208.96) * mm, v(1.34, 209.23) * mm]});
            skLineSegment(sketch, "E288", {"start": v(1.34, 209.23) * mm, "end": v(0.84, 209.73) * mm});
            skLineSegment(sketch, "E289", {"start": v(0.84, 209.73) * mm, "end": v(0.45, 209.73) * mm});
            skLineSegment(sketch, "E290", {"start": v(0.45, 209.73) * mm, "end": v(0.18, 209.73) * mm});
            skLineSegment(sketch, "E291", {"start": v(0.18, 209.73) * mm, "end": v(0.3, 210.83) * mm});
            skFitSpline(sketch, "E292", {"points": [v(0.3, 210.83) * mm, v(0.33, 211.17) * mm, v(0.42, 211.95) * mm, v(0.68, 213.16) * mm]});
            skLineSegment(sketch, "E293", {"start": v(0.68, 213.16) * mm, "end": v(1.1, 215.36) * mm});
            skFitSpline(sketch, "E294", {"points": [v(1.1, 215.36) * mm, v(1.13, 215.87) * mm, v(0.38, 216.25) * mm, v(0.01, 215.25) * mm]});
            skLineSegment(sketch, "E295", {"start": v(-122.38, -47.81) * mm, "end": v(-69.67, -87.08) * mm});
            skLineSegment(sketch, "E296", {"start": v(92.08, -157.19) * mm, "end": v(70.2, -86.82) * mm});
            skSolve(sketch);
        }
        {
            var Q0;
            Q0=makeQuery(id+"F0.imprint","IMPRINT",FACE,{"disambiguationData":[TD([[makeQuery(id+"F0.imprint","IMPRINT",EDGE,{"derivedFrom":sQuery(id+"F0.wireOp",EDGE,"E0")}),1.0]])]});
            extrude(context, id + "F1", {"entities" : qUnion([Q0]), "depth" : 25 * mm});
        }
    });
